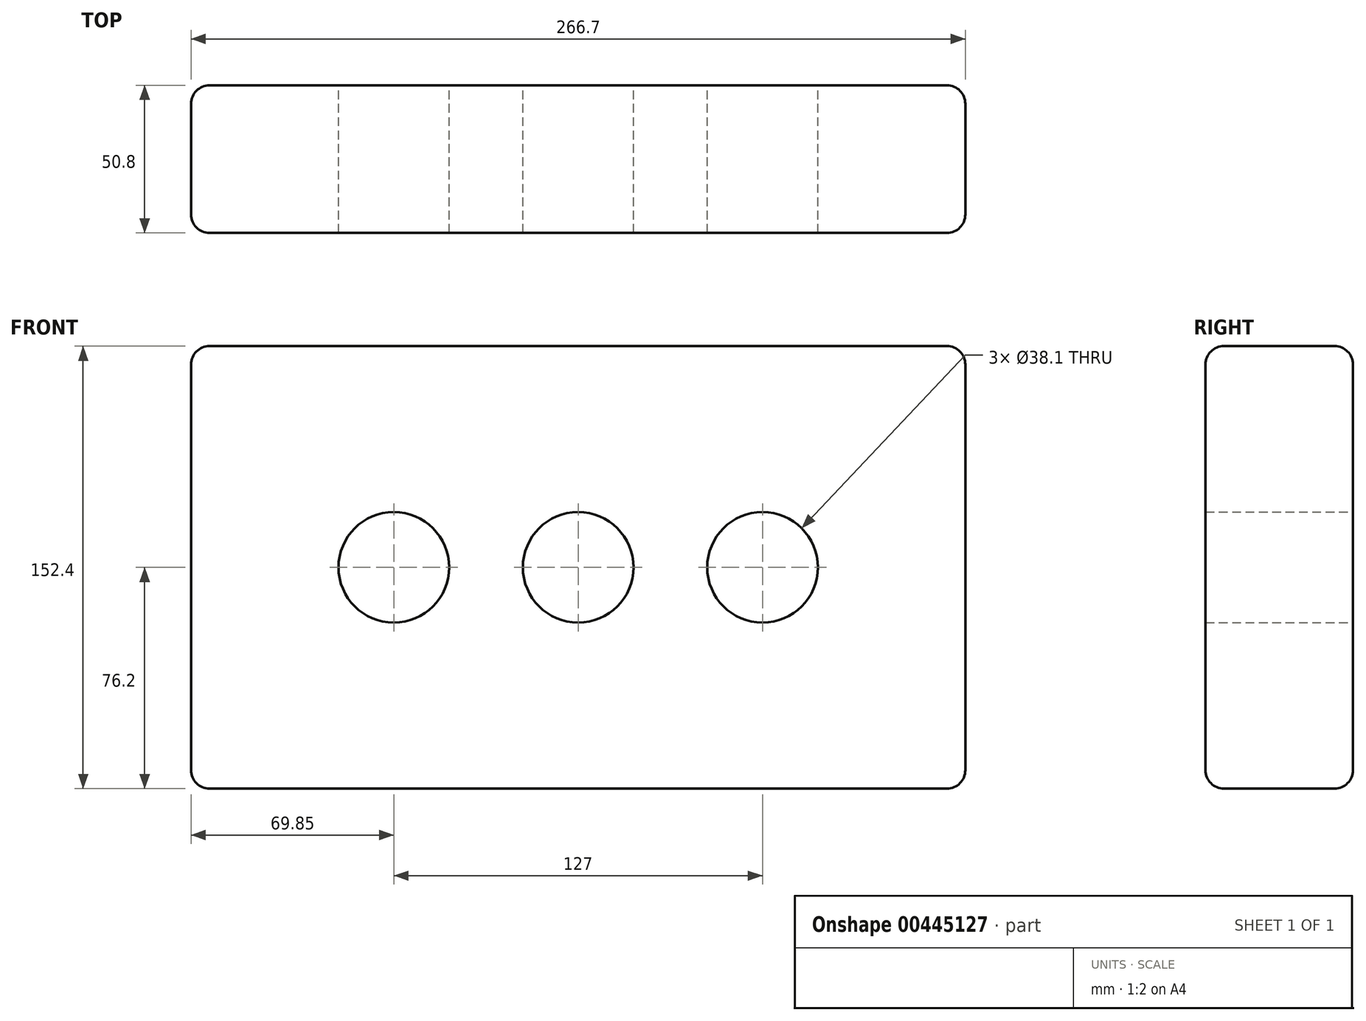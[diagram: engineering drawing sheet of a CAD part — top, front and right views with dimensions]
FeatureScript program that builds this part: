
annotation { "Feature Type Name" : "Feature", "Feature Type Description" : "" }
export const myFeature = defineFeature(function(context is Context, id is Id, definition is map)
    precondition{}
    {
        {
            var Q0;
            Q0=qCreatedBy(makeId("Front.planeOp"),FACE);
            var sketch = newSketch(context, id + "F0", { "sketchPlane" : qUnion([Q0])});
            skLineSegment(sketch, "E0.bottom", {"start": v(133.35, 76.2) * mm, "end": v(-133.35, 76.2) * mm});
            skLineSegment(sketch, "E0.top", {"start": v(133.35, -76.2) * mm, "end": v(-133.35, -76.2) * mm});
            skLineSegment(sketch, "E0.left", {"start": v(133.35, 76.2) * mm, "end": v(133.35, -76.2) * mm});
            skLineSegment(sketch, "E0.right", {"start": v(-133.35, 76.2) * mm, "end": v(-133.35, -76.2) * mm});
            skPoint(sketch, "E0.middle", {"position": v(0, 0) * mm});
            skCircle(sketch, "E1", {"center": v(0, 0) * mm, "radius": 19.05 * mm});
            skCircle(sketch, "E2", {"center": v(63.5, 0) * mm, "radius": 19.05 * mm});
            skCircle(sketch, "E3", {"center": v(-63.5, 0) * mm, "radius": 19.05 * mm});
            skSolve(sketch);
        }
        {
            var Q0;
            Q0=makeQuery(id+"F0.imprint","IMPRINT",FACE,{"disambiguationData":[TD([[makeQuery(id+"F0.imprint","IMPRINT",EDGE,{"derivedFrom":sQuery(id+"F0.wireOp",EDGE,"E0.bottom")}),1.0]])]});
            extrude(context, id + "F1", {"entities" : qUnion([Q0]), "depth" : 50.8 * mm});
        }
        {
            var Q0;
            Q0=makeQuery(id+"F1.opExtrude","CAP_EDGE",EDGE,{"disambiguationData":[OSD([sQuery(id+"F0.wireOp",EDGE,"E0.bottom")])],"isStart":false});
            fillet(context, id + "F2", {"entities" : qUnion([Q0]), "radius" : 6.35 * mm, "tangentPropagation" : true, "allowEdgeOverflow" : false});
        }
        {
            var Q0;
            Q0=makeQuery(id+"F1.opExtrude","CAP_EDGE",EDGE,{"disambiguationData":[OSD([sQuery(id+"F0.wireOp",EDGE,"E0.left")])],"isStart":false});
            fillet(context, id + "F3", {"entities" : qUnion([Q0]), "radius" : 6.35 * mm, "tangentPropagation" : true, "allowEdgeOverflow" : false});
        }
        {
            var Q0;
            Q0=makeQuery(id+"F1.opExtrude","CAP_EDGE",EDGE,{"disambiguationData":[OSD([sQuery(id+"F0.wireOp",EDGE,"E0.top")])],"isStart":false});
            var Q1;
            Q1=makeQuery(id+"F1.opExtrude","CAP_EDGE",EDGE,{"disambiguationData":[OSD([sQuery(id+"F0.wireOp",EDGE,"E0.right")])],"isStart":false});
            fillet(context, id + "F4", {"entities" : qUnion([Q0, Q1]), "radius" : 6.35 * mm, "tangentPropagation" : true, "allowEdgeOverflow" : false});
        }
        {
            var Q0;
            Q0=makeQuery(id+"F1.opExtrude","CAP_EDGE",EDGE,{"disambiguationData":[OSD([sQuery(id+"F0.wireOp",EDGE,"E0.bottom")])],"isStart":true});
            fillet(context, id + "F5", {"entities" : qUnion([Q0]), "radius" : 6.35 * mm, "tangentPropagation" : true, "allowEdgeOverflow" : false});
        }
        {
            var Q0;
            Q0=makeQuery(id+"F1.opExtrude","SWEPT_EDGE",EDGE,{"disambiguationData":[OSD([sQuery(id+"F0.wireOp",EDGE,"E0.top"),sQuery(id+"F0.wireOp",EDGE,"E0.right")])]});
            fillet(context, id + "F6", {"entities" : qUnion([Q0]), "radius" : 6.35 * mm, "tangentPropagation" : true, "allowEdgeOverflow" : false});
        }
    });
